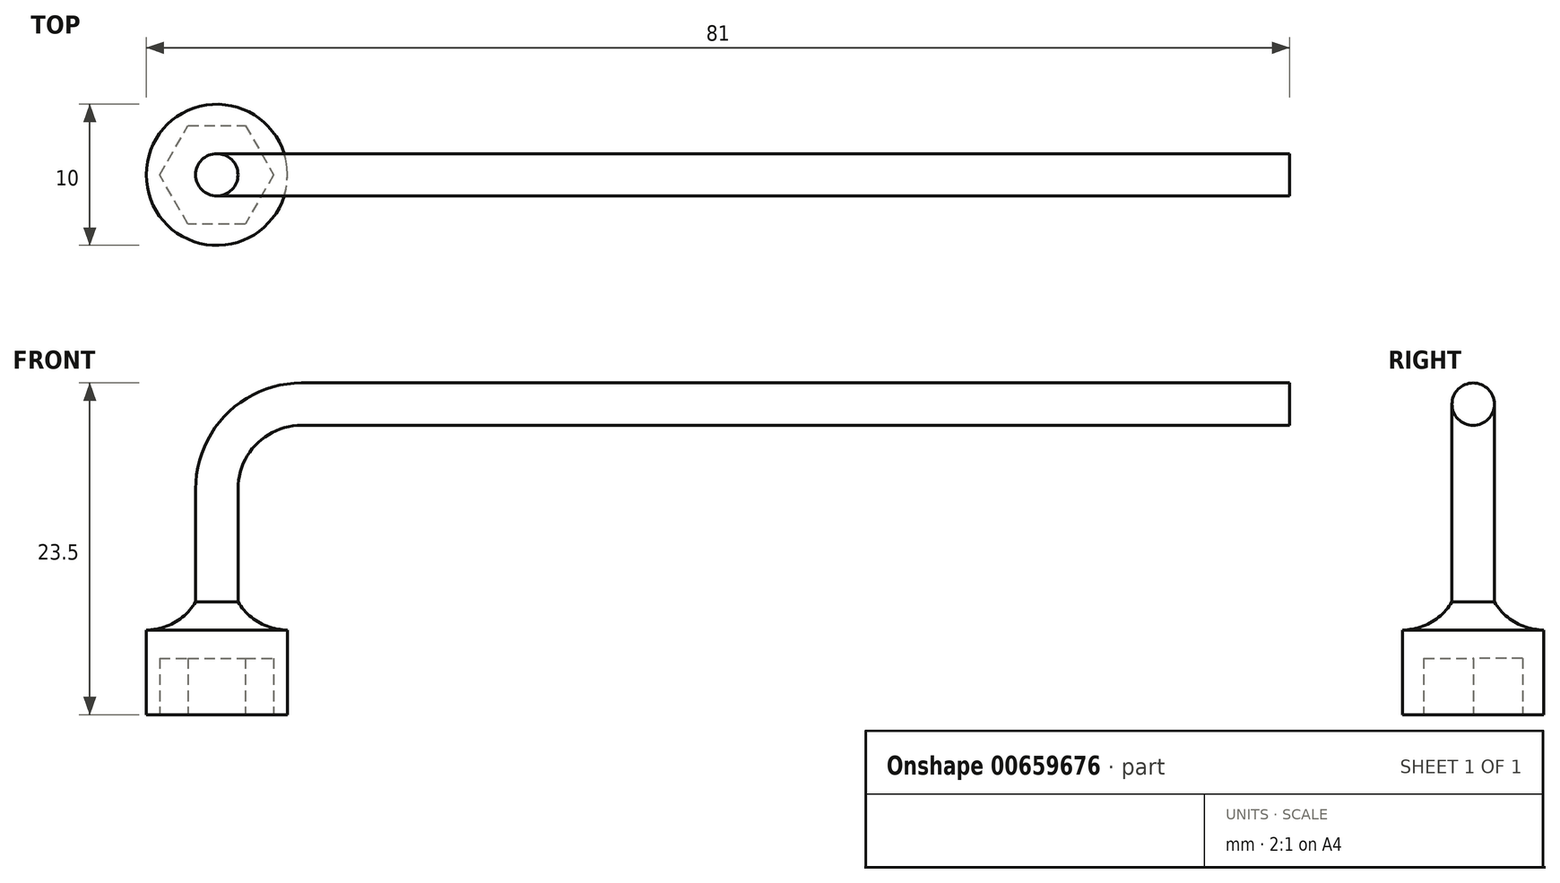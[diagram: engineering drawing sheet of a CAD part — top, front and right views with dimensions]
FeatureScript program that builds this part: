
annotation { "Feature Type Name" : "Feature", "Feature Type Description" : "" }
export const myFeature = defineFeature(function(context is Context, id is Id, definition is map)
    precondition{}
    {
        {
            var Q0;
            Q0=qCreatedBy(makeId("Front.planeOp"),FACE);
            var sketch = newSketch(context, id + "F0", { "sketchPlane" : qUnion([Q0])});
            skLineSegment(sketch, "E0", {"start": v(50, 22) * mm, "end": v(-20, 22) * mm});
            skLineSegment(sketch, "E1", {"start": v(-26, 0) * mm, "end": v(-26, 6) * mm});
            skLineSegment(sketch, "E2.bottom", {"start": v(-31, 6) * mm, "end": v(-21, 6) * mm});
            skLineSegment(sketch, "E2.top", {"start": v(-31, 0) * mm, "end": v(-21, 0) * mm});
            skLineSegment(sketch, "E2.left", {"start": v(-31, 6) * mm, "end": v(-31, 0) * mm});
            skLineSegment(sketch, "E2.right", {"start": v(-21, 6) * mm, "end": v(-21, 0) * mm});
            skLineSegment(sketch, "E3", {"start": v(-26, 6) * mm, "end": v(-26, 8) * mm});
            skLineSegment(sketch, "E4", {"start": v(-26, 8) * mm, "end": v(-27.5, 8) * mm});
            skLineSegment(sketch, "E5", {"start": v(-27.5, 8) * mm, "end": v(-24.5, 8) * mm});
            skArc(sketch, "E6", {"start": v(-31, 6) * mm, "mid": v(-28.98, 6.54) * mm, "end": v(-27.5, 8) * mm});
            skLineSegment(sketch, "E7", {"start": v(-26, 8) * mm, "end": v(-26, 16) * mm});
            skArc(sketch, "E8", {"start": v(-20, 22) * mm, "mid": v(-24.24, 20.24) * mm, "end": v(-26, 16) * mm});
            skSolve(sketch);
        }
        {
            var Q0;
            Q0=qCreatedBy(makeId("Top.planeOp"),FACE);
            var sketch = newSketch(context, id + "F1", { "sketchPlane" : qUnion([Q0])});
            skCircle(sketch, "E9.cCircle", {"center": v(-26.01, 0) * mm, "radius": 3.5 * mm, "construction": true});
            skLineSegment(sketch, "E9.0", {"start": v(-24, 3.5) * mm, "end": v(-21.97, 0) * mm});
            skLineSegment(sketch, "E9.1", {"start": v(-21.97, 0) * mm, "end": v(-24, -3.5) * mm});
            skLineSegment(sketch, "E9.2", {"start": v(-24, -3.5) * mm, "end": v(-28.03, -3.5) * mm});
            skLineSegment(sketch, "E9.3", {"start": v(-28.03, -3.5) * mm, "end": v(-30.05, 0) * mm});
            skLineSegment(sketch, "E9.4", {"start": v(-30.05, 0) * mm, "end": v(-28.03, 3.5) * mm});
            skLineSegment(sketch, "E9.5", {"start": v(-28.03, 3.5) * mm, "end": v(-24, 3.5) * mm});
            skPoint(sketch, "E9.0.midPoint", {"position": v(-22.98, 1.75) * mm});
            skCircle(sketch, "E10", {"center": v(-26.01, 0) * mm, "radius": 5 * mm});
            skSolve(sketch);
        }
        {
            var Q0;
            {var subQ0=sQuery(id+"F0.wireOp",EDGE,"E1");Q0=makeQuery(id+"F0.imprint","IMPRINT",FACE,{"disambiguationData":[TD([[makeQuery(id+"F0.imprint","IMPRINT",EDGE,{"derivedFrom":subQ0}),1.0]])]});}
            var Q1;
            Q1=sQuery(id+"F0.wireOp",EDGE,"E1");
            revolve(context, id + "F2", {"entities" : qUnion([Q0]), "axis" : qUnion([Q1]), "revolveType" : RevolveType.FULL});
        }
        {
            var Q0;
            Q0=makeQuery(id+"F1.imprint","IMPRINT",FACE,{"disambiguationData":[TD([[makeQuery(id+"F1.imprint","IMPRINT",EDGE,{"derivedFrom":sQuery(id+"F1.wireOp",EDGE,"E9.0")}),-1.0]])]});
            extrude(context, id + "F3", {"entities" : qUnion([Q0]), "operationType" : NewBodyOperationType.REMOVE, "depth" : 4 * mm, "offsetDistance" : 25 * mm});
        }
        {
            var Q0;
            Q0=qCreatedBy(makeId("Right.planeOp"),FACE);
            var sketch = newSketch(context, id + "F4", { "sketchPlane" : qUnion([Q0])});
            skCircle(sketch, "E11", {"center": v(0, 22) * mm, "radius": 1.5 * mm});
            skSolve(sketch);
        }
        {
            var Q0;
            Q0=makeQuery(id+"F4.imprint","IMPRINT",FACE,{"disambiguationData":[TD([[makeQuery(id+"F4.imprint","IMPRINT",EDGE,{"derivedFrom":sQuery(id+"F4.wireOp",EDGE,"E11")}),1.0]])]});
            var Q1;
            Q1=sQuery(id+"F0.wireOp",EDGE,"E0");
            var Q2;
            Q2=sQuery(id+"F0.wireOp",EDGE,"z1r6iJkD-9MSs-snZ7-aaY1-B0AFt3OxdYvc");
            sweep(context, id + "F5", {"operationType" : NewBodyOperationType.ADD, "profiles" : qUnion([Q0]), "path" : qUnion([Q1, Q2])});
        }
        {
            var Q0;
            {var subQ0=sQuery(id+"F0.wireOp",EDGE,"E3");Q0=makeQuery(id+"F0.imprint","IMPRINT",FACE,{"disambiguationData":[TD([[makeQuery(id+"F0.imprint","IMPRINT",EDGE,{"derivedFrom":subQ0}),1.0]])]});}
            var Q1;
            Q1=sQuery(id+"F0.wireOp",EDGE,"E3");
            revolve(context, id + "F6", {"operationType" : NewBodyOperationType.ADD, "entities" : qUnion([Q0]), "axis" : qUnion([Q1]), "revolveType" : RevolveType.FULL});
        }
        {
            var Q0;
            Q0=makeQuery(id+"F5.opSweep","CAP_FACE",FACE,{"disambiguationData":[OSD([sQuery(id+"F0.wireOp",VERTEX,"E0.start"),sQuery(id+"F4.wireOp",EDGE,"E11")])],"isStart":false});
            var sketch = newSketch(context, id + "F7", { "sketchPlane" : qUnion([Q0])});
            skText(sketch, "E12", { "text": "RRDT", "fontName": "OpenSans-Regular.ttf"});
            const initialGuessF7  = {"E12": [-0.00108, 0.0117, 1, 0, 0.0006]};
            skSetInitialGuess(sketch, initialGuessF7);
            skSolve(sketch);
        }
        {
            var Q0;
            Q0=makeQuery(id+"F5.opSweep","CAP_FACE",FACE,{"disambiguationData":[OSD([sQuery(id+"F0.wireOp",VERTEX,"E0.end"),sQuery(id+"F4.wireOp",EDGE,"E11")])],"isStart":true});
            var Q1;
            Q1=sQuery(id+"F0.wireOp",EDGE,"E8");
            var Q2;
            Q2=sQuery(id+"F0.wireOp",EDGE,"E7");
            sweep(context, id + "F8", {"operationType" : NewBodyOperationType.ADD, "profiles" : qUnion([Q0]), "path" : qUnion([Q1, Q2])});
        }
        {
            var Q0;
            Q0 = qSketchRegion(id + "F7", true);
            extrude(context, id + "F9", {"entities" : qUnion([Q0]), "operationType" : NewBodyOperationType.REMOVE, "oppositeDirection" : true, "depth" : 5 * mm, "offsetDistance" : 25 * mm});
        }
    });
